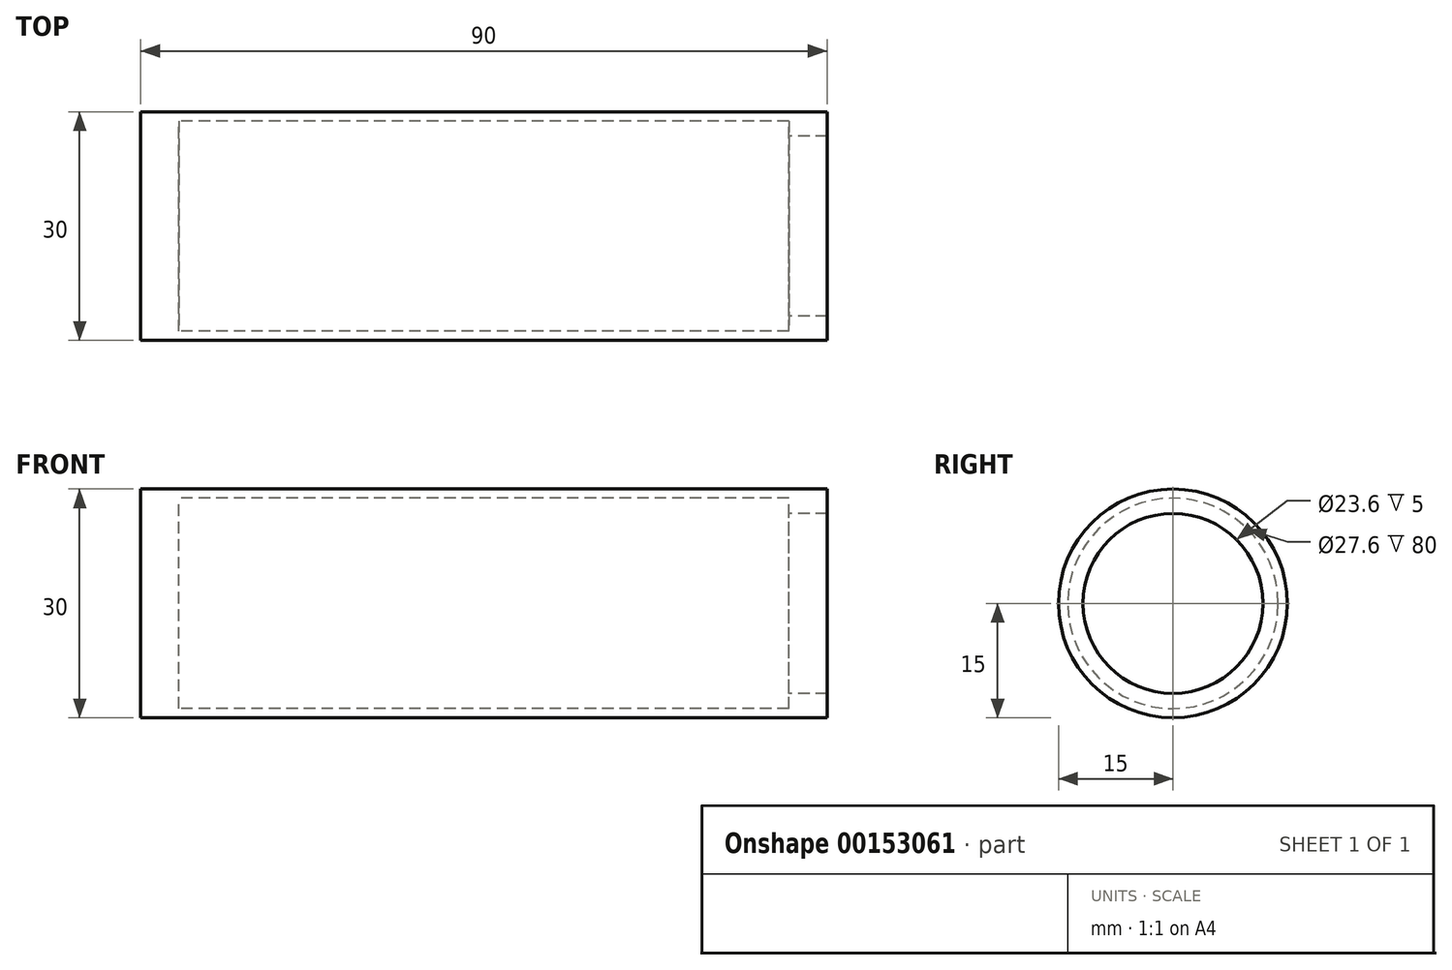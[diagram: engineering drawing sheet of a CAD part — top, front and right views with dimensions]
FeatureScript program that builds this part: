
annotation { "Feature Type Name" : "Feature", "Feature Type Description" : "" }
export const myFeature = defineFeature(function(context is Context, id is Id, definition is map)
    precondition{}
    {
        {
            var Q0;
            Q0=qCreatedBy(makeId("Right.planeOp"),FACE);
            var sketch = newSketch(context, id + "F0", { "sketchPlane" : qUnion([Q0])});
            skCircle(sketch, "E0", {"center": v(0, 0) * mm, "radius": 15 * mm});
            skCircle(sketch, "E1.0", {"center": v(0, 0) * mm, "radius": 13.8 * mm});
            skSolve(sketch);
        }
        {
            var Q0;
            Q0=makeQuery(id+"F0.imprint","IMPRINT",FACE,{"disambiguationData":[TD([[makeQuery(id+"F0.imprint","IMPRINT",EDGE,{"derivedFrom":sQuery(id+"F0.wireOp",EDGE,"E0")}),1.0]])]});
            var Q1;
            Q1=makeQuery(id+"F0.imprint","IMPRINT",FACE,{"disambiguationData":[TD([[makeQuery(id+"F0.imprint","IMPRINT",EDGE,{"derivedFrom":sQuery(id+"F0.wireOp",EDGE,"E1.0")}),1.0]])]});
            extrude(context, id + "F1", {"entities" : qUnion([Q0, Q1]), "depth" : 5 * mm});
        }
        {
            var Q0;
            Q0=makeQuery(id+"F1.opExtrude","CAP_FACE",FACE,{"disambiguationData":[OSD([sQuery(id+"F0.wireOp",EDGE,"E0")])],"isStart":false});
            var sketch = newSketch(context, id + "F2", { "sketchPlane" : qUnion([Q0])});
            skCircle(sketch, "E2.0", {"center": v(0, 0) * mm, "radius": 13.8 * mm});
            skSolve(sketch);
        }
        {
            var Q0;
            Q0=makeQuery(id+"F2.imprint","IMPRINT",FACE,{"disambiguationData":[TD([[makeQuery(id+"F2.imprint","IMPRINT",EDGE,{"derivedFrom":sQuery(id+"F2.wireOp",EDGE,"E2.0")}),-1.0]])]});
            extrude(context, id + "F3", {"entities" : qUnion([Q0]), "operationType" : NewBodyOperationType.ADD, "depth" : 80 * mm});
        }
        {
            var Q0;
            Q0=makeQuery(id+"F3.opExtrude","CAP_FACE",FACE,{"disambiguationData":[OSD([sQuery(id+"F0.wireOp",EDGE,"E0"),sQuery(id+"F2.wireOp",EDGE,"E2.0")])],"isStart":false});
            var sketch = newSketch(context, id + "F4", { "sketchPlane" : qUnion([Q0])});
            skCircle(sketch, "E3.0", {"center": v(0, 0) * mm, "radius": 11.8 * mm});
            skSolve(sketch);
        }
        {
            var Q0;
            Q0=makeQuery(id+"F4.imprint","IMPRINT",FACE,{"disambiguationData":[TD([[makeQuery(id+"F4.imprint","IMPRINT",EDGE,{"derivedFrom":sQuery(id+"F4.wireOp",EDGE,"E3.0")}),-1.0]])]});
            var Q1;
            Q1=makeQuery(id+"F4.imprint","IMPRINT",FACE,{"disambiguationData":[TD([[makeQuery(id+"F4.imprint","IMPRINT",EDGE,{"derivedFrom":makeQuery(id+"F3.opExtrude","CAP_EDGE",EDGE,{"disambiguationData":[OSD([sQuery(id+"F2.wireOp",EDGE,"E2.0")])],"isStart":false})}),-1.0]])]});
            extrude(context, id + "F5", {"entities" : qUnion([Q0, Q1]), "operationType" : NewBodyOperationType.ADD, "depth" : 5 * mm});
        }
    });
